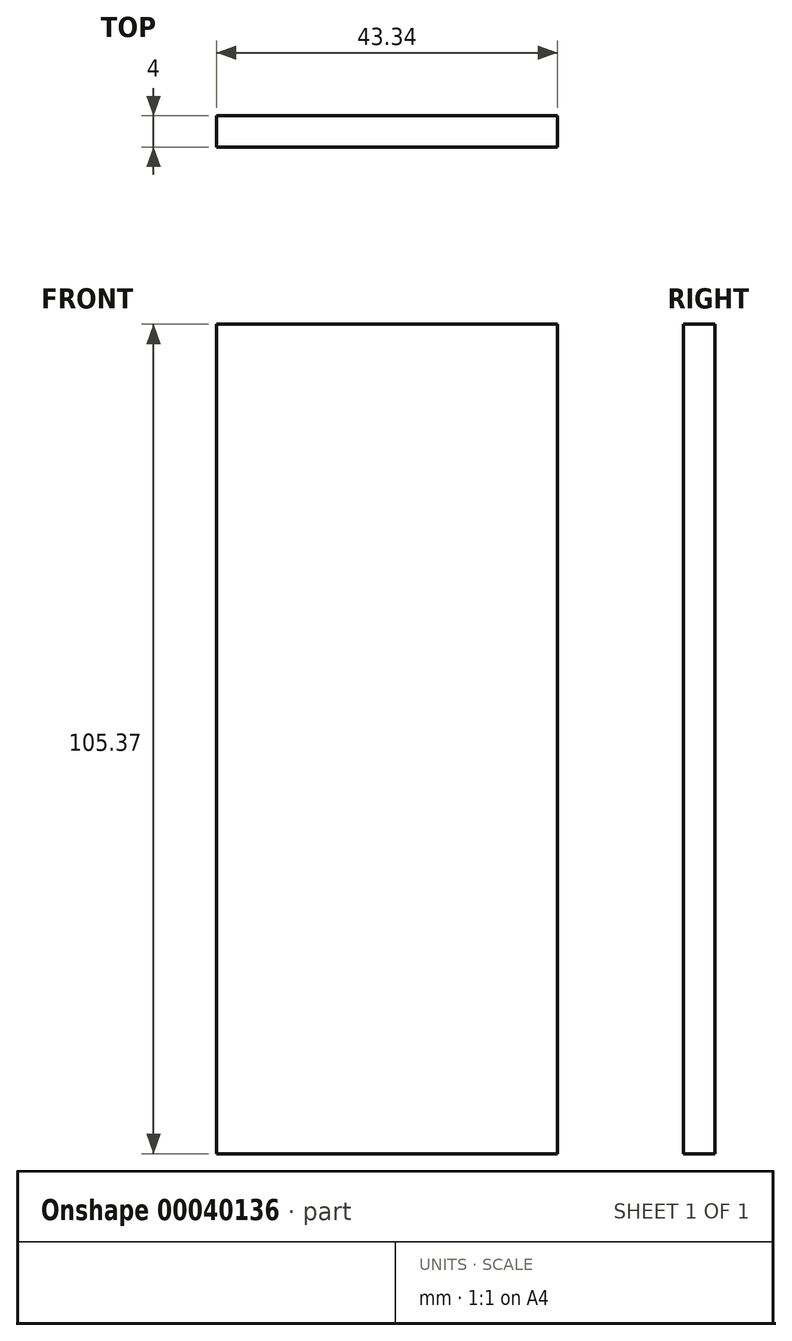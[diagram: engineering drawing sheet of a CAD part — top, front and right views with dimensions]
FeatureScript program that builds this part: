
annotation { "Feature Type Name" : "Feature", "Feature Type Description" : "" }
export const myFeature = defineFeature(function(context is Context, id is Id, definition is map)
    precondition{}
    {
        {
            var Q0;
            Q0=qCreatedBy(makeId("Front.planeOp"),FACE);
            var sketch = newSketch(context, id + "F0", { "sketchPlane" : qUnion([Q0])});
            skLineSegment(sketch, "E0.bottom", {"start": v(-28.47, 34.13) * mm, "end": v(14.87, 34.13) * mm});
            skLineSegment(sketch, "E0.top", {"start": v(-28.47, -71.24) * mm, "end": v(14.87, -71.24) * mm});
            skLineSegment(sketch, "E0.left", {"start": v(-28.47, 34.13) * mm, "end": v(-28.47, -71.24) * mm});
            skLineSegment(sketch, "E0.right", {"start": v(14.87, 34.13) * mm, "end": v(14.87, -71.24) * mm});
            skSolve(sketch);
        }
        {
            var Q0;
            Q0 = qSketchRegion(id + "F0", true);
            extrude(context, id + "F1", {"entities" : qUnion([Q0]), "depth" : 4 * mm, "offsetDistance" : 25 * mm});
        }
    });
